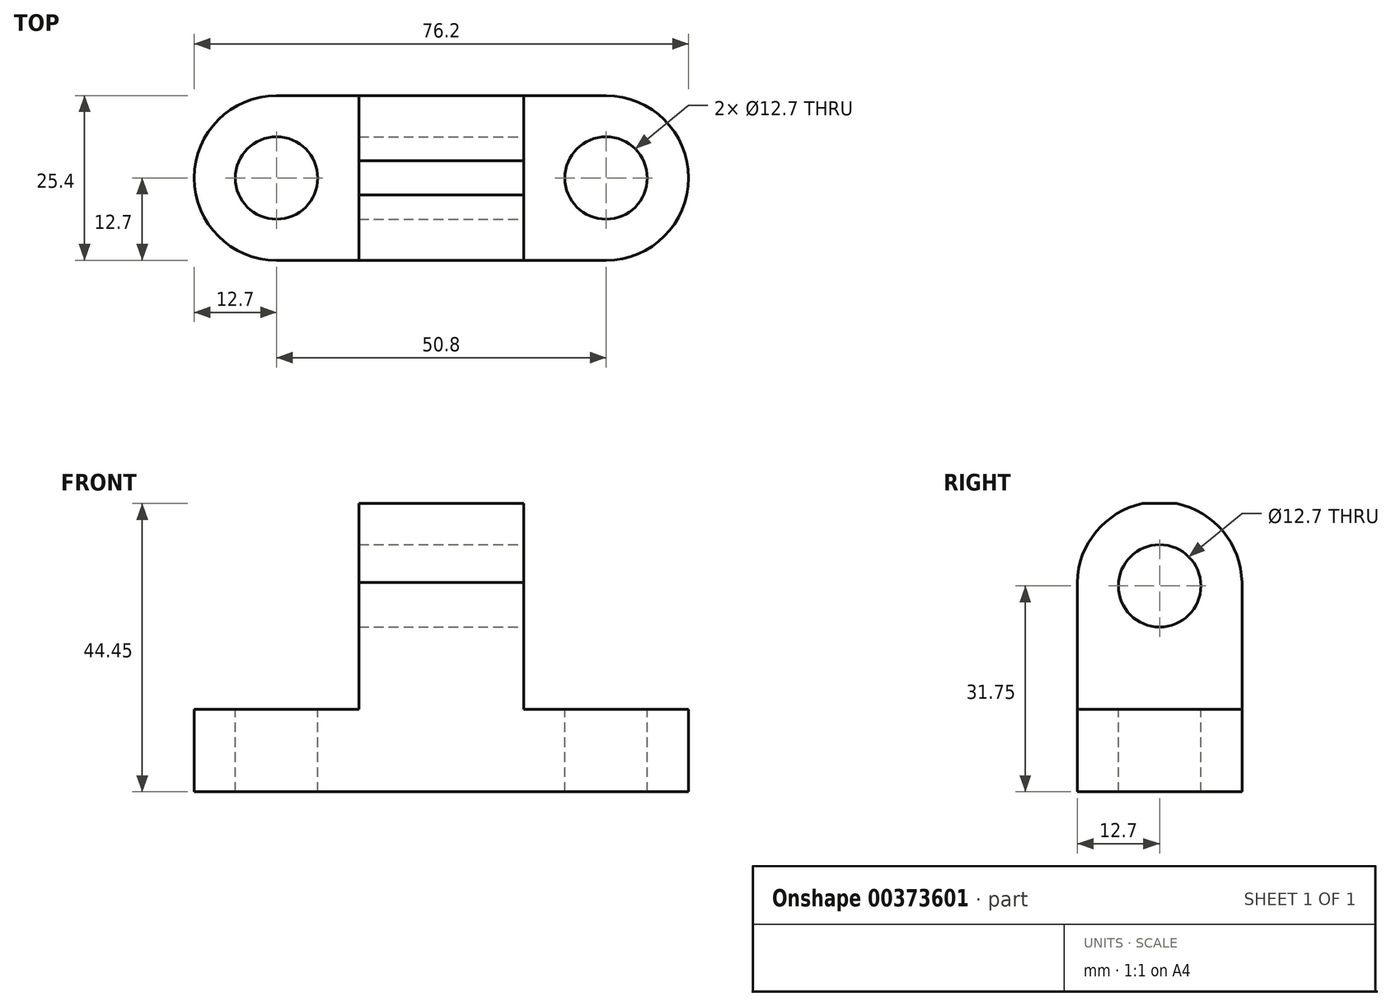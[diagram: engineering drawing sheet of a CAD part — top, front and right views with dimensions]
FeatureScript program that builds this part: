
annotation { "Feature Type Name" : "Feature", "Feature Type Description" : "" }
export const myFeature = defineFeature(function(context is Context, id is Id, definition is map)
    precondition{}
    {
        {
            var Q0;
            Q0=qCreatedBy(makeId("Front.planeOp"),FACE);
            var sketch = newSketch(context, id + "F0", { "sketchPlane" : qUnion([Q0])});
            skLineSegment(sketch, "E0", {"start": v(0, 0) * mm, "end": v(0, 12.7) * mm});
            skLineSegment(sketch, "E1", {"start": v(0, 12.7) * mm, "end": v(25.4, 12.7) * mm});
            skLineSegment(sketch, "E2", {"start": v(25.4, 12.7) * mm, "end": v(25.4, 44.45) * mm});
            skLineSegment(sketch, "E3", {"start": v(25.4, 44.45) * mm, "end": v(50.8, 44.45) * mm});
            skLineSegment(sketch, "E4", {"start": v(50.8, 44.45) * mm, "end": v(50.8, 12.7) * mm});
            skLineSegment(sketch, "E5", {"start": v(50.8, 12.7) * mm, "end": v(76.2, 12.7) * mm});
            skLineSegment(sketch, "E6", {"start": v(76.2, 12.7) * mm, "end": v(76.2, 0) * mm});
            skLineSegment(sketch, "E7", {"start": v(76.2, 0) * mm, "end": v(0, 0) * mm});
            skSolve(sketch);
        }
        {
            var Q0;
            Q0 = qSketchRegion(id + "F0", true);
            extrude(context, id + "F1", {"entities" : qUnion([Q0]), "depth" : 25.4 * mm});
        }
        {
            var Q0;
            Q0=makeQuery(id+"F1.opExtrude","SWEPT_FACE",FACE,{"disambiguationData":[OSD([sQuery(id+"F0.wireOp",EDGE,"E4")])]});
            var sketch = newSketch(context, id + "F2", { "sketchPlane" : qUnion([Q0])});
            skCircle(sketch, "E8", {"center": v(-12.7, 31.75) * mm, "radius": 6.35 * mm});
            skArc(sketch, "E9", {"start": v(0, 31.75) * mm, "mid": v(-12.7, 44.73) * mm, "end": v(-25.4, 31.75) * mm});
            skSolve(sketch);
        }
        {
            var Q0;
            {var subQ0=sQuery(id+"F2.wireOp",EDGE,"E9");var subQ1=sQuery(id+"F0.wireOp",EDGE,"E4");var subQ4=makeQuery(id+"F1.opExtrude","CAP_EDGE",EDGE,{"disambiguationData":[OSD([subQ1])],"isStart":false});var subQ5=makeQuery(id+"F2.imprint","INTERSECT",VERTEX,{"disambiguationData":[OD(1.0)],"derivedFrom":[subQ4,subQ0]});Q0=makeQuery(id+"F2.imprint","IMPRINT",FACE,{"disambiguationData":[TD([[makeQuery(id+"F2.imprint","IMPRINT",EDGE,{"disambiguationData":[TD([[subQ5,1.0]])],"derivedFrom":subQ0}),-1.0]])]});}
            var Q1;
            {var subQ0=sQuery(id+"F2.wireOp",EDGE,"E9");var subQ1=sQuery(id+"F0.wireOp",EDGE,"E4");var subQ2=makeQuery(id+"F1.opExtrude","CAP_EDGE",EDGE,{"disambiguationData":[OSD([subQ1])],"isStart":true});var subQ3=makeQuery(id+"F2.imprint","INTERSECT",VERTEX,{"disambiguationData":[OD(1.0)],"derivedFrom":[subQ2,subQ0]});Q1=makeQuery(id+"F2.imprint","IMPRINT",FACE,{"disambiguationData":[TD([[makeQuery(id+"F2.imprint","IMPRINT",EDGE,{"disambiguationData":[TD([[subQ3,-1.0]])],"derivedFrom":subQ0}),-1.0]])]});}
            var Q2;
            Q2=makeQuery(id+"F2.imprint","IMPRINT",FACE,{"disambiguationData":[TD([[makeQuery(id+"F2.imprint","IMPRINT",EDGE,{"derivedFrom":sQuery(id+"F2.wireOp",EDGE,"E8")}),1.0]])]});
            extrude(context, id + "F3", {"entities" : qUnion([Q0, Q1, Q2]), "operationType" : NewBodyOperationType.REMOVE, "oppositeDirection" : true, "depth" : 25.4 * mm});
        }
        {
            var Q0;
            Q0=makeQuery(id+"F1.opExtrude","SWEPT_FACE",FACE,{"disambiguationData":[OSD([sQuery(id+"F0.wireOp",EDGE,"E5")])]});
            var sketch = newSketch(context, id + "F4", { "sketchPlane" : qUnion([Q0])});
            skCircle(sketch, "E10", {"center": v(63.5, -12.7) * mm, "radius": 6.35 * mm});
            skPoint(sketch, "E10.centerSnap0", {"position": v(50.8, -12.7) * mm});
            skArc(sketch, "E11", {"start": v(63.5, -25.4) * mm, "mid": v(76.2, -12.7) * mm, "end": v(63.5, 0) * mm});
            skSolve(sketch);
        }
        {
            var Q0;
            {var subQ0=sQuery(id+"F4.wireOp",EDGE,"E11");var subQ1=sQuery(id+"F0.wireOp",EDGE,"E5");var subQ2=makeQuery(id+"F1.opExtrude","CAP_EDGE",EDGE,{"disambiguationData":[OSD([subQ1])],"isStart":true});var subQ3=makeQuery(id+"F4.imprint","INTERSECT",VERTEX,{"derivedFrom":[subQ2,subQ0]});Q0=makeQuery(id+"F4.imprint","IMPRINT",FACE,{"disambiguationData":[TD([[makeQuery(id+"F4.imprint","IMPRINT",EDGE,{"disambiguationData":[TD([[subQ3,1.0]])],"derivedFrom":subQ0}),-1.0]])]});}
            var Q1;
            {var subQ0=sQuery(id+"F4.wireOp",EDGE,"E11");var subQ1=sQuery(id+"F0.wireOp",EDGE,"E5");var subQ2=makeQuery(id+"F1.opExtrude","CAP_EDGE",EDGE,{"disambiguationData":[OSD([subQ1])],"isStart":false});var subQ3=makeQuery(id+"F4.imprint","INTERSECT",VERTEX,{"derivedFrom":[subQ2,subQ0]});Q1=makeQuery(id+"F4.imprint","IMPRINT",FACE,{"disambiguationData":[TD([[makeQuery(id+"F4.imprint","IMPRINT",EDGE,{"disambiguationData":[TD([[subQ3,-1.0]])],"derivedFrom":subQ0}),-1.0]])]});}
            var Q2;
            Q2=makeQuery(id+"F4.imprint","IMPRINT",FACE,{"disambiguationData":[TD([[makeQuery(id+"F4.imprint","IMPRINT",EDGE,{"derivedFrom":sQuery(id+"F4.wireOp",EDGE,"E10")}),1.0]])]});
            extrude(context, id + "F5", {"entities" : qUnion([Q0, Q1, Q2]), "operationType" : NewBodyOperationType.REMOVE, "oppositeDirection" : true, "depth" : 25.4 * mm});
        }
        {
            var Q0;
            Q0=makeQuery(id+"F1.opExtrude","SWEPT_FACE",FACE,{"disambiguationData":[OSD([sQuery(id+"F0.wireOp",EDGE,"E1")])]});
            var sketch = newSketch(context, id + "F6", { "sketchPlane" : qUnion([Q0])});
            skCircle(sketch, "E12", {"center": v(12.7, -12.7) * mm, "radius": 6.35 * mm});
            skArc(sketch, "E13", {"start": v(12.7, 0) * mm, "mid": v(0, -12.7) * mm, "end": v(12.7, -25.4) * mm});
            skSolve(sketch);
        }
        {
            var Q0;
            Q0=makeQuery(id+"F6.imprint","IMPRINT",FACE,{"disambiguationData":[TD([[makeQuery(id+"F6.imprint","IMPRINT",EDGE,{"derivedFrom":sQuery(id+"F6.wireOp",EDGE,"E12")}),1.0]])]});
            var Q1;
            {var subQ0=sQuery(id+"F6.wireOp",EDGE,"E13");var subQ1=sQuery(id+"F0.wireOp",EDGE,"E1");var subQ2=makeQuery(id+"F1.opExtrude","CAP_EDGE",EDGE,{"disambiguationData":[OSD([subQ1])],"isStart":true});var subQ3=makeQuery(id+"F6.imprint","INTERSECT",VERTEX,{"derivedFrom":[subQ2,subQ0]});Q1=makeQuery(id+"F6.imprint","IMPRINT",FACE,{"disambiguationData":[TD([[makeQuery(id+"F6.imprint","IMPRINT",EDGE,{"disambiguationData":[TD([[subQ3,-1.0]])],"derivedFrom":subQ0}),-1.0]])]});}
            var Q2;
            {var subQ0=sQuery(id+"F6.wireOp",EDGE,"E13");var subQ1=sQuery(id+"F0.wireOp",EDGE,"E1");var subQ2=makeQuery(id+"F1.opExtrude","CAP_EDGE",EDGE,{"disambiguationData":[OSD([subQ1])],"isStart":false});var subQ3=makeQuery(id+"F6.imprint","INTERSECT",VERTEX,{"derivedFrom":[subQ2,subQ0]});Q2=makeQuery(id+"F6.imprint","IMPRINT",FACE,{"disambiguationData":[TD([[makeQuery(id+"F6.imprint","IMPRINT",EDGE,{"disambiguationData":[TD([[subQ3,1.0]])],"derivedFrom":subQ0}),-1.0]])]});}
            extrude(context, id + "F7", {"entities" : qUnion([Q0, Q1, Q2]), "operationType" : NewBodyOperationType.REMOVE, "oppositeDirection" : true, "depth" : 25.4 * mm});
        }
    });
